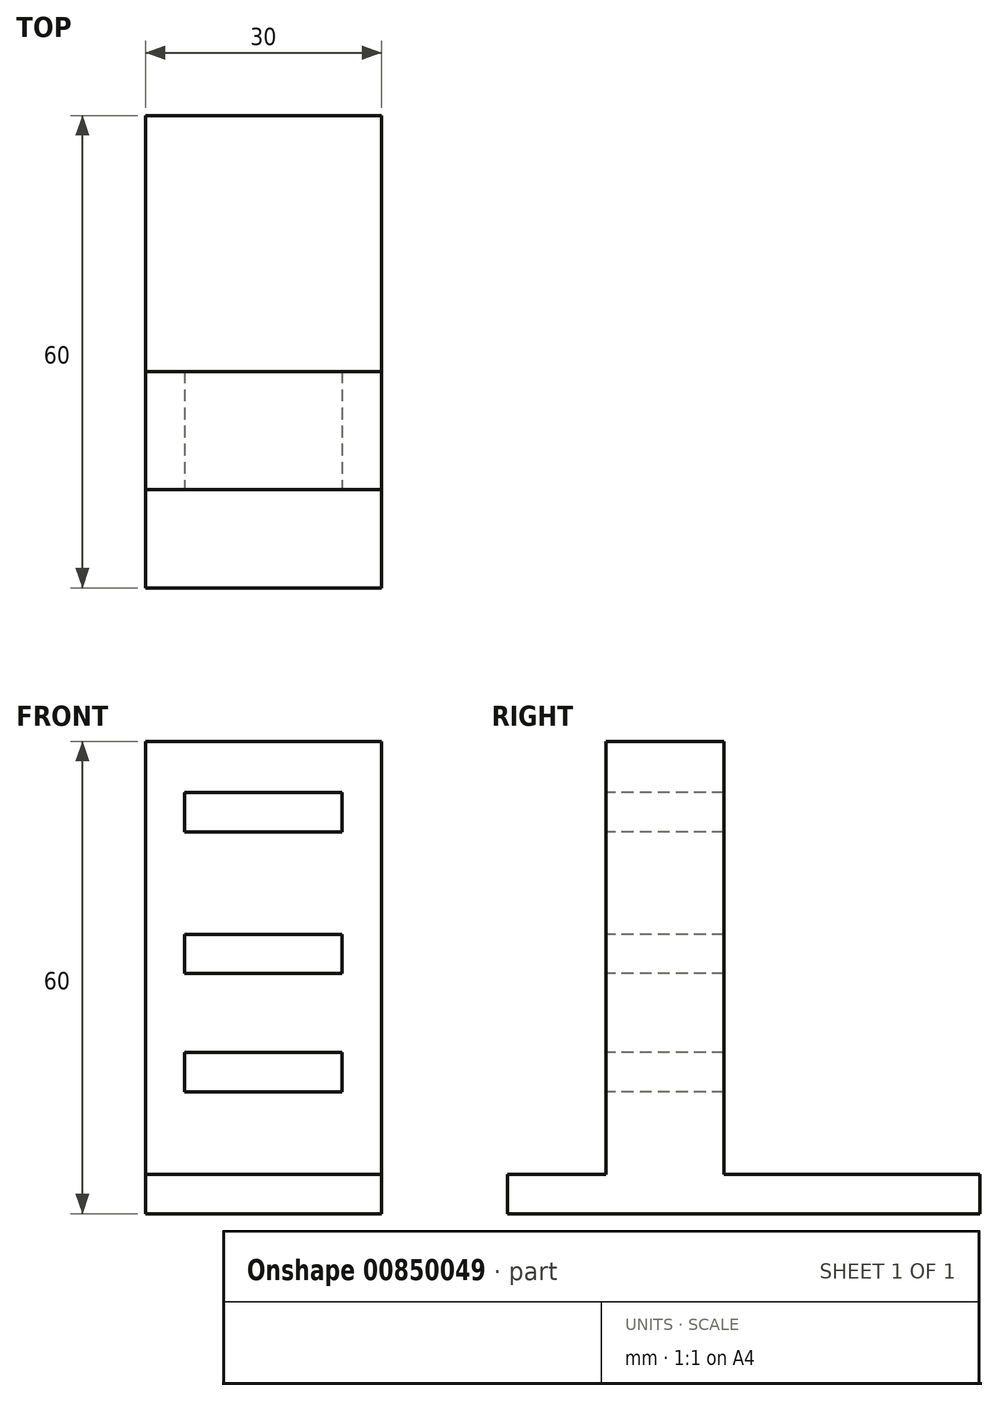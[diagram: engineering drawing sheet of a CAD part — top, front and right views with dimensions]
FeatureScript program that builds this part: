
annotation { "Feature Type Name" : "Feature", "Feature Type Description" : "" }
export const myFeature = defineFeature(function(context is Context, id is Id, definition is map)
    precondition{}
    {
        {
            assignVariable(context, id + "F0", {"name" : "AlturaBase", "anyValue" : 5});
        }
        {
            assignVariable(context, id + "F1", {"name" : "AlturaTotal", "anyValue" : 60});
        }
        {
            var Q0;
            Q0=qCreatedBy(makeId("Top.planeOp"),FACE);
            var sketch = newSketch(context, id + "F2", { "sketchPlane" : qUnion([Q0])});
            skLineSegment(sketch, "E0.bottom", {"start": v(-15, 40) * mm, "end": v(15, 40) * mm});
            skLineSegment(sketch, "E0.top", {"start": v(-15, -20) * mm, "end": v(15, -20) * mm});
            skLineSegment(sketch, "E0.left", {"start": v(-15, 40) * mm, "end": v(-15, -20) * mm});
            skLineSegment(sketch, "E0.right", {"start": v(15, 40) * mm, "end": v(15, -20) * mm});
            skSolve(sketch);
        }
        {
            var Q0;
            Q0 = qSketchRegion(id + "F2", true);
            extrude(context, id + "F3", {"entities" : qUnion([Q0]), "depth" : (getVariable(context, 'AlturaBase')) * mm, "offsetDistance" : 25 * mm});
        }
        {
            var Q0;
            Q0=makeQuery(id+"F3.opExtrude","CAP_FACE",FACE,{"disambiguationData":[OSD([sQuery(id+"F2.wireOp",EDGE,"E0.bottom"),sQuery(id+"F2.wireOp",EDGE,"E0.top"),sQuery(id+"F2.wireOp",EDGE,"E0.left"),sQuery(id+"F2.wireOp",EDGE,"E0.right")])],"isStart":false});
            var sketch = newSketch(context, id + "F4", { "sketchPlane" : qUnion([Q0])});
            skLineSegment(sketch, "E1.bottom", {"start": v(15, 7.5) * mm, "end": v(-15, 7.5) * mm});
            skLineSegment(sketch, "E1.top", {"start": v(15, -7.5) * mm, "end": v(-15, -7.5) * mm});
            skLineSegment(sketch, "E1.left", {"start": v(15, 7.5) * mm, "end": v(15, -7.5) * mm});
            skLineSegment(sketch, "E1.right", {"start": v(-15, 7.5) * mm, "end": v(-15, -7.5) * mm});
            skPoint(sketch, "E1.middle", {"position": v(0, 0) * mm});
            skSolve(sketch);
        }
        {
            var Q0;
            Q0=makeQuery(id+"F4.imprint","IMPRINT",FACE,{"disambiguationData":[TD([[makeQuery(id+"F4.imprint","IMPRINT",EDGE,{"derivedFrom":sQuery(id+"F4.wireOp",EDGE,"E1.bottom")}),1.0]])]});
            extrude(context, id + "F5", {"entities" : qUnion([Q0]), "operationType" : NewBodyOperationType.ADD, "depth" : ((getVariable(context, 'AlturaTotal')) - getVariable(context, 'AlturaBase')) * mm, "offsetDistance" : 25 * mm});
        }
        {
            var Q0;
            Q0=makeQuery(id+"F5.opExtrude","SWEPT_FACE",FACE,{"disambiguationData":[OSD([sQuery(id+"F4.wireOp",EDGE,"E1.top")])]});
            var sketch = newSketch(context, id + "F6", { "sketchPlane" : qUnion([Q0])});
            skLineSegment(sketch, "E2.bottom", {"start": v(10, 20.5) * mm, "end": v(-10, 20.5) * mm});
            skLineSegment(sketch, "E2.top", {"start": v(10, 15.5) * mm, "end": v(-10, 15.5) * mm});
            skLineSegment(sketch, "E2.left", {"start": v(10, 20.5) * mm, "end": v(10, 15.5) * mm});
            skLineSegment(sketch, "E2.right", {"start": v(-10, 20.5) * mm, "end": v(-10, 15.5) * mm});
            skPoint(sketch, "E2.middle", {"position": v(0, 18) * mm});
            skLineSegment(sketch, "E3.bottom", {"start": v(10, 35.5) * mm, "end": v(-10, 35.5) * mm});
            skLineSegment(sketch, "E3.top", {"start": v(10, 30.5) * mm, "end": v(-10, 30.5) * mm});
            skLineSegment(sketch, "E3.left", {"start": v(10, 35.5) * mm, "end": v(10, 30.5) * mm});
            skLineSegment(sketch, "E3.right", {"start": v(-10, 35.5) * mm, "end": v(-10, 30.5) * mm});
            skPoint(sketch, "E3.middle", {"position": v(0, 33) * mm});
            skLineSegment(sketch, "E4.bottom", {"start": v(10, 53.5) * mm, "end": v(-10, 53.5) * mm});
            skLineSegment(sketch, "E4.top", {"start": v(10, 48.5) * mm, "end": v(-10, 48.5) * mm});
            skLineSegment(sketch, "E4.left", {"start": v(10, 53.5) * mm, "end": v(10, 48.5) * mm});
            skLineSegment(sketch, "E4.right", {"start": v(-10, 53.5) * mm, "end": v(-10, 48.5) * mm});
            skPoint(sketch, "E4.middle", {"position": v(0, 51) * mm});
            skSolve(sketch);
        }
        {
            var Q0;
            Q0=makeQuery(id+"F6.imprint","IMPRINT",FACE,{"disambiguationData":[TD([[makeQuery(id+"F6.imprint","IMPRINT",EDGE,{"derivedFrom":sQuery(id+"F6.wireOp",EDGE,"E4.bottom")}),1.0]])]});
            var Q1;
            Q1=makeQuery(id+"F6.imprint","IMPRINT",FACE,{"disambiguationData":[TD([[makeQuery(id+"F6.imprint","IMPRINT",EDGE,{"derivedFrom":sQuery(id+"F6.wireOp",EDGE,"E3.bottom")}),1.0]])]});
            var Q2;
            Q2=makeQuery(id+"F6.imprint","IMPRINT",FACE,{"disambiguationData":[TD([[makeQuery(id+"F6.imprint","IMPRINT",EDGE,{"derivedFrom":sQuery(id+"F6.wireOp",EDGE,"E2.bottom")}),1.0]])]});
            extrude(context, id + "F7", {"entities" : qUnion([Q0, Q1, Q2]), "operationType" : NewBodyOperationType.REMOVE, "endBound" : BoundingType.THROUGH_ALL, "oppositeDirection" : true, "depth" : 25 * mm, "offsetDistance" : 25 * mm});
        }
    });
